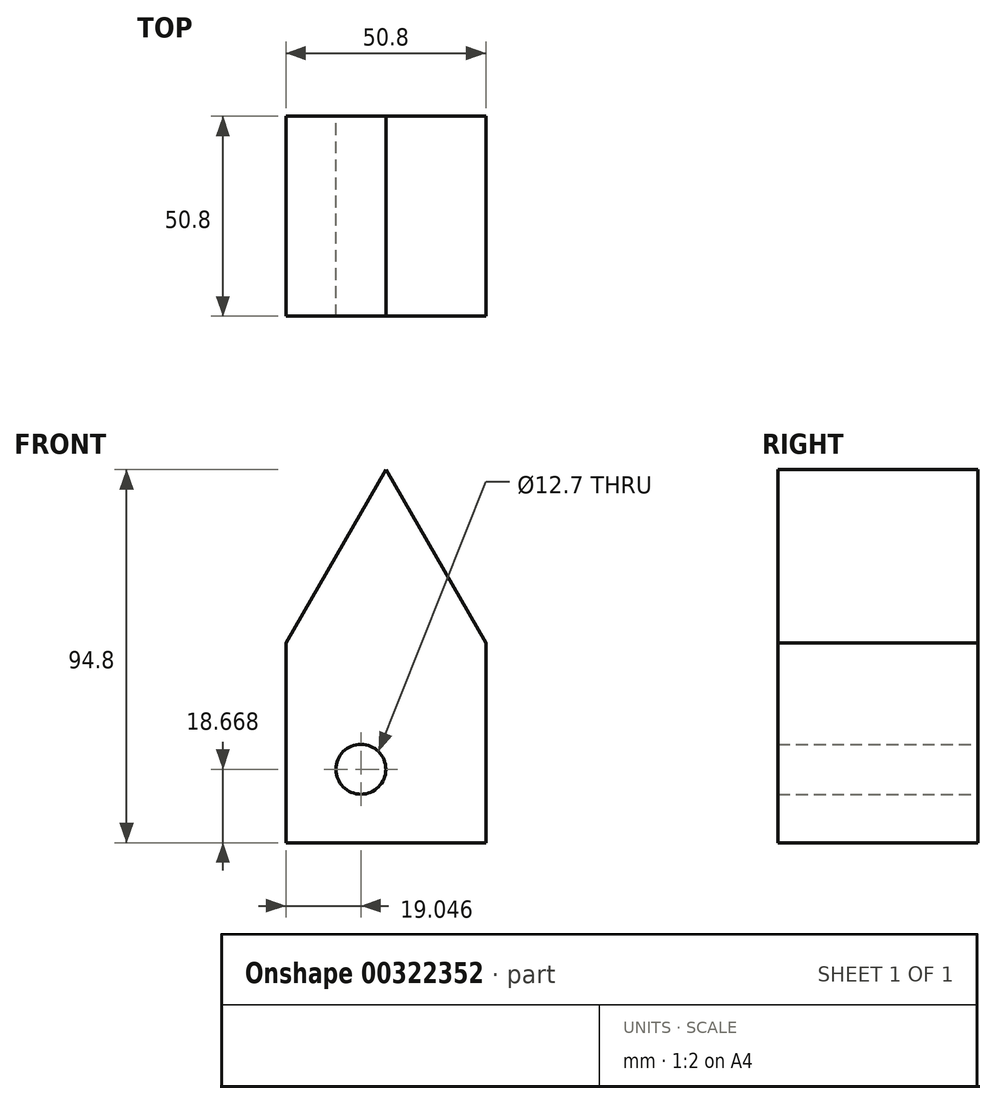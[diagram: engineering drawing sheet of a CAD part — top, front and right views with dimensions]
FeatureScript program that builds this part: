
annotation { "Feature Type Name" : "Feature", "Feature Type Description" : "" }
export const myFeature = defineFeature(function(context is Context, id is Id, definition is map)
    precondition{}
    {
        {
            var Q0;
            Q0=qCreatedBy(makeId("Front.planeOp"),FACE);
            var sketch = newSketch(context, id + "F0", { "sketchPlane" : qUnion([Q0])});
            skLineSegment(sketch, "E0.bottom", {"start": v(-20.47, -26.03) * mm, "end": v(30.33, -26.03) * mm});
            skLineSegment(sketch, "E0.left", {"start": v(-20.47, -26.03) * mm, "end": v(-20.47, 24.77) * mm});
            skLineSegment(sketch, "E0.right", {"start": v(30.33, -26.03) * mm, "end": v(30.33, 24.77) * mm});
            skLineSegment(sketch, "E1", {"start": v(-20.47, 24.77) * mm, "end": v(4.93, 68.77) * mm});
            skLineSegment(sketch, "E2", {"start": v(4.93, 68.77) * mm, "end": v(30.33, 24.77) * mm});
            skLineSegment(sketch, "E3.0", {"start": v(30.71, -26.41) * mm, "end": v(30.71, 24.77) * mm});
            skLineSegment(sketch, "E3.1", {"start": v(-20.86, -26.41) * mm, "end": v(30.71, -26.41) * mm});
            skLineSegment(sketch, "E3.2", {"start": v(-20.86, -26.41) * mm, "end": v(-20.86, 24.77) * mm});
            skCircle(sketch, "E4", {"center": v(-1.42, -7.36) * mm, "radius": 6.35 * mm});
            skSolve(sketch);
        }
        {
            var Q0;
            Q0=makeQuery(id+"F0.imprint","IMPRINT",FACE,{"disambiguationData":[TD([[makeQuery(id+"F0.imprint","IMPRINT",EDGE,{"derivedFrom":sQuery(id+"F0.wireOp",EDGE,"E0.bottom")}),1.0]])]});
            extrude(context, id + "F1", {"entities" : qUnion([Q0]), "depth" : 50.8 * mm});
        }
    });
